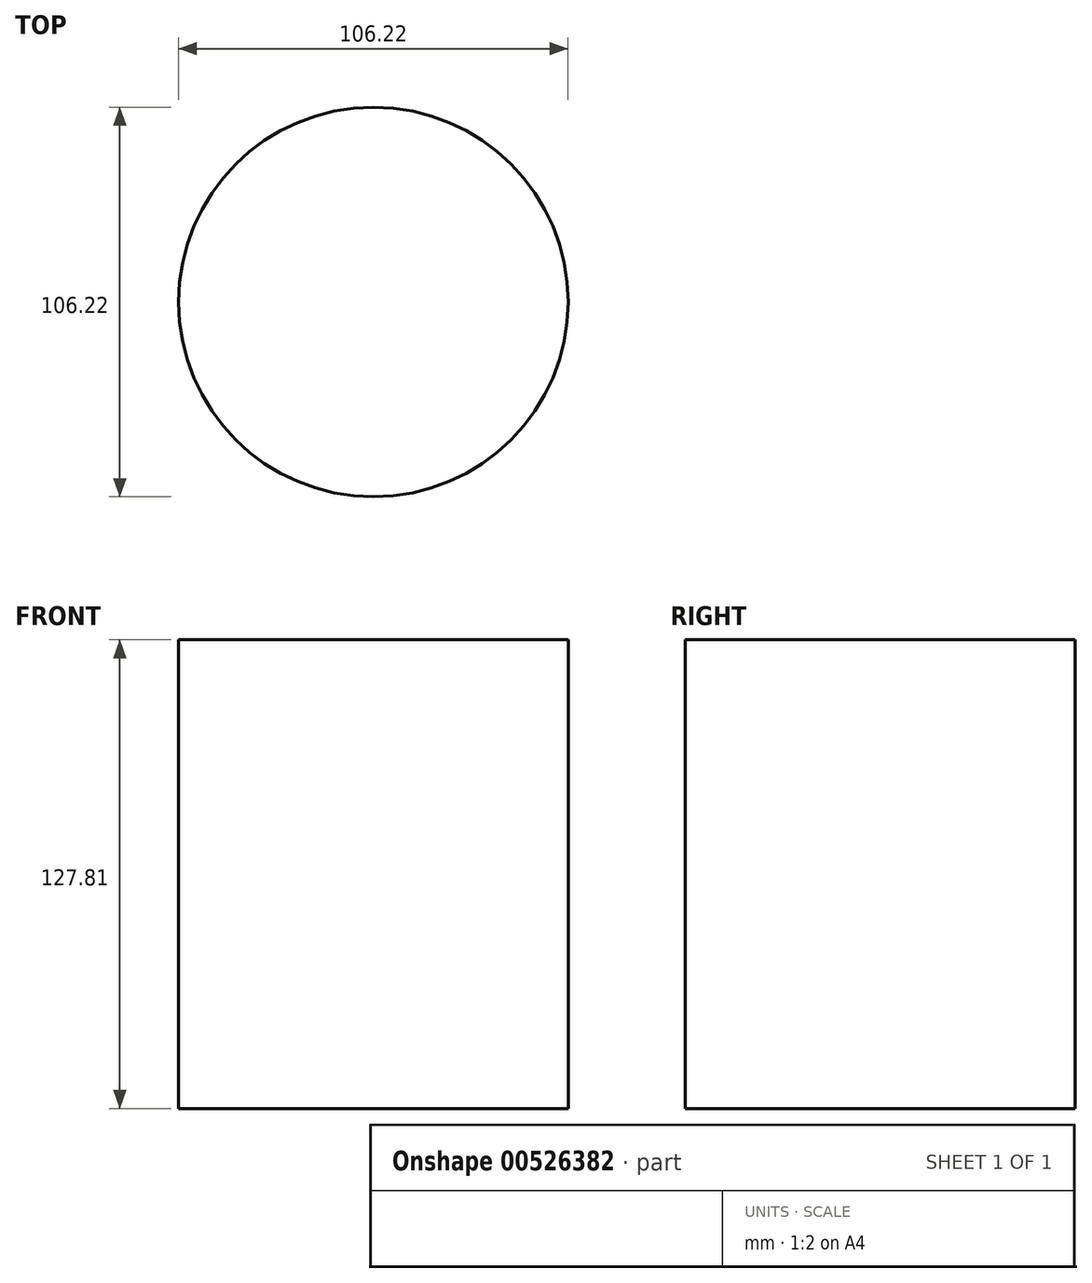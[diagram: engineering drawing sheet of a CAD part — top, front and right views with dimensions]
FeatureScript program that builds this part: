
annotation { "Feature Type Name" : "Feature", "Feature Type Description" : "" }
export const myFeature = defineFeature(function(context is Context, id is Id, definition is map)
    precondition{}
    {
        {
            var Q0;
            Q0=qCreatedBy(makeId("Top.planeOp"),FACE);
            var sketch = newSketch(context, id + "F0", { "sketchPlane" : qUnion([Q0])});
            skCircle(sketch, "E0", {"center": v(46.04, 0) * mm, "radius": 53.11 * mm});
            skSolve(sketch);
        }
        {
            var Q0;
            Q0=makeQuery(id+"F0.imprint","IMPRINT",FACE,{"disambiguationData":[TD([[makeQuery(id+"F0.imprint","IMPRINT",EDGE,{"derivedFrom":sQuery(id+"F0.wireOp",EDGE,"E0")}),1.0]])]});
            var sketch = newSketch(context, id + "F1", { "sketchPlane" : qUnion([Q0])});
            skSolve(sketch);
        }
        {
            var Q0;
            Q0=makeQuery(id+"F1.imprint","IMPRINT",FACE,{"disambiguationData":[TD([[makeQuery(id+"F1.imprint","IMPRINT",EDGE,{"derivedFrom":makeQuery(id+"F0.imprint","IMPRINT",EDGE,{"derivedFrom":sQuery(id+"F0.wireOp",EDGE,"E0")})}),1.0]])]});
            extrude(context, id + "F2", {"entities" : qUnion([Q0]), "depth" : 127.81 * mm, "offsetDistance" : 25.4 * mm});
        }
    });
